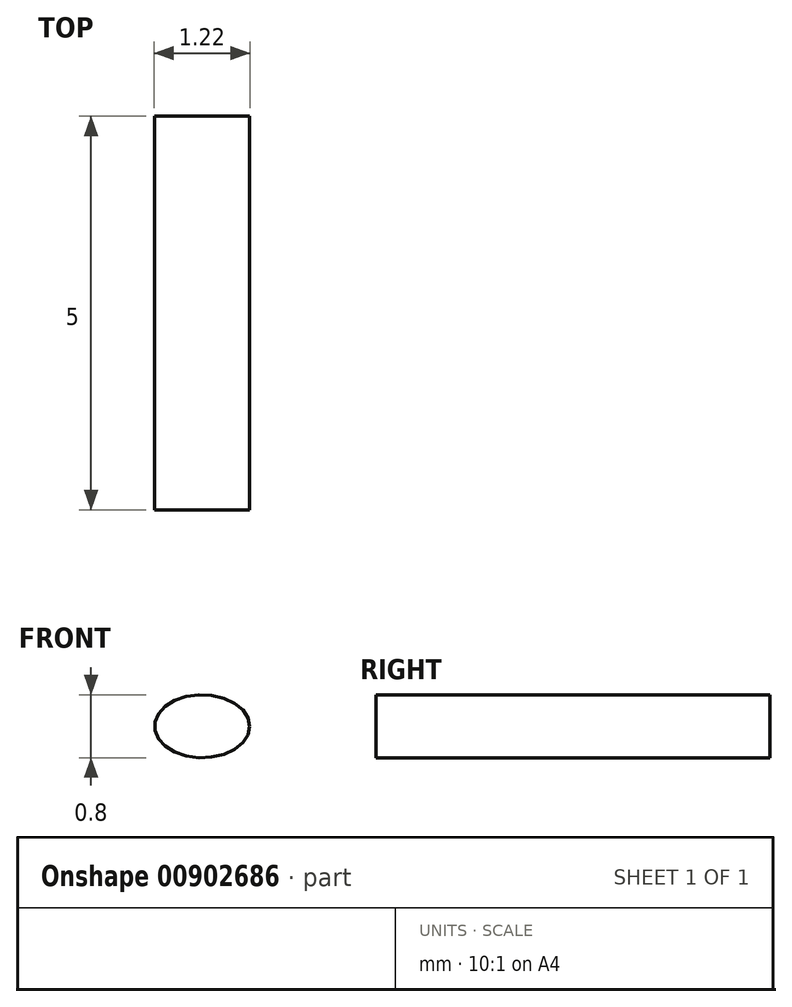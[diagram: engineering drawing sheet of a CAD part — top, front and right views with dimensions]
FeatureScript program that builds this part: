
annotation { "Feature Type Name" : "Feature", "Feature Type Description" : "" }
export const myFeature = defineFeature(function(context is Context, id is Id, definition is map)
    precondition{}
    {
        {
            var Q0;
            Q0=qCreatedBy(makeId("Front.planeOp"),FACE);
            var sketch = newSketch(context, id + "F0", { "sketchPlane" : qUnion([Q0])});
            skEllipse(sketch, "E0", {"center": v(0, 0) * mm, "majorRadius": 0.6 * mm, "minorRadius": 0.4 * mm, "majorAxis": v(1, 0)});
            skSolve(sketch);
        }
        {
            var Q0;
            Q0 = qSketchRegion(id + "F0", true);
            extrude(context, id + "F1", {"entities" : qUnion([Q0]), "depth" : 5 * mm, "offsetDistance" : 25.4 * mm});
        }
    });
